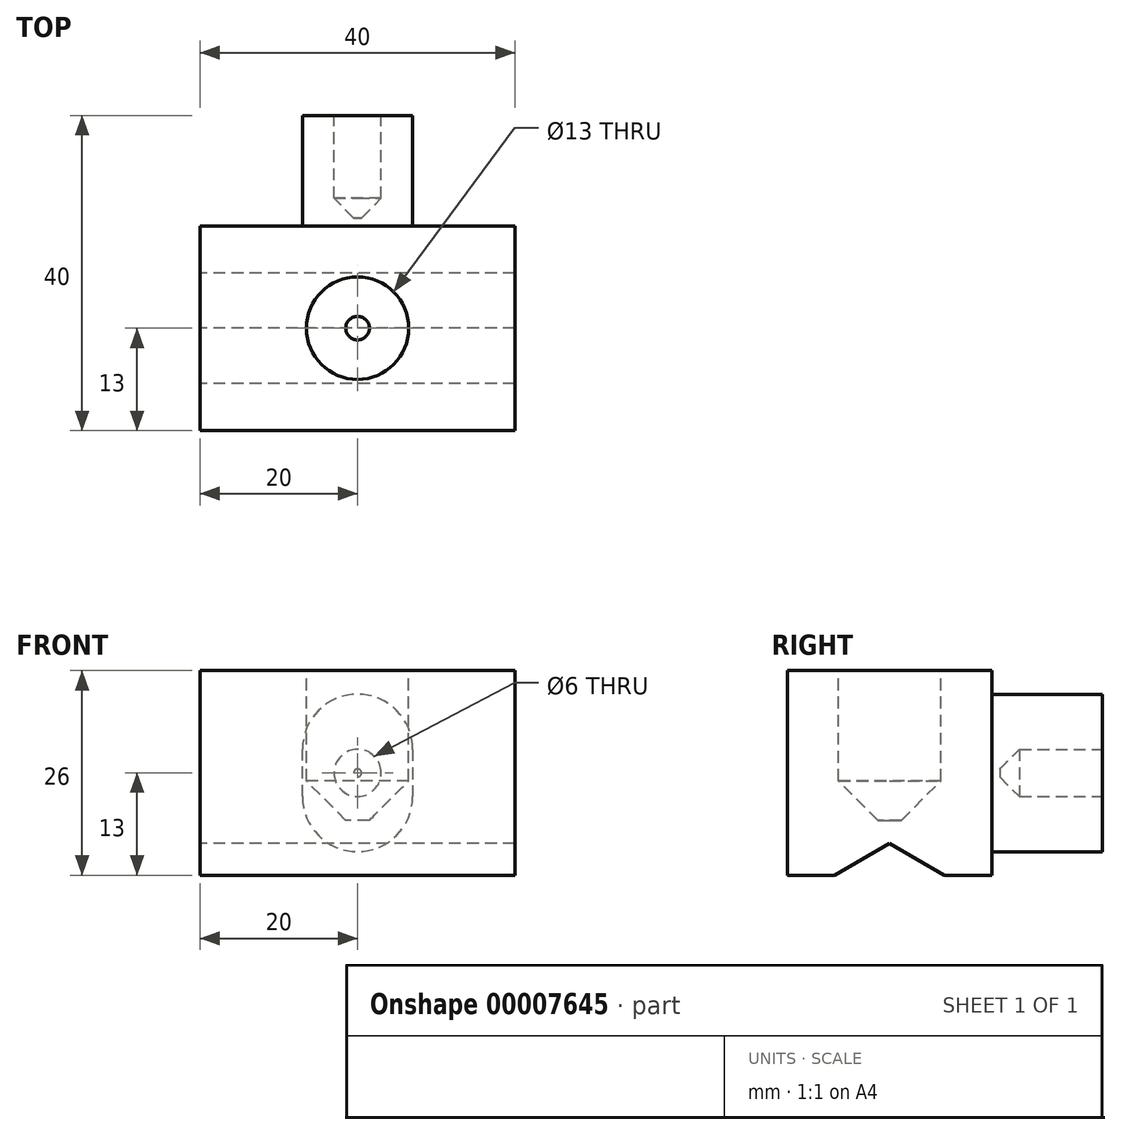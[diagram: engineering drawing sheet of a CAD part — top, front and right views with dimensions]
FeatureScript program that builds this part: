
annotation { "Feature Type Name" : "Feature", "Feature Type Description" : "" }
export const myFeature = defineFeature(function(context is Context, id is Id, definition is map)
    precondition{}
    {
        {
            var Q0;
            Q0=qCreatedBy(makeId("Right.planeOp"),FACE);
            var sketch = newSketch(context, id + "F0", { "sketchPlane" : qUnion([Q0])});
            skLineSegment(sketch, "E0.rect.bottom", {"start": v(-13, -13) * mm, "end": v(-7, -13) * mm});
            skLineSegment(sketch, "E0.rect.top", {"start": v(-13, 13) * mm, "end": v(13, 13) * mm});
            skLineSegment(sketch, "E0.rect.left", {"start": v(-13, -13) * mm, "end": v(-13, 13) * mm});
            skLineSegment(sketch, "E0.rect.right", {"start": v(13, -13) * mm, "end": v(13, 13) * mm});
            skPoint(sketch, "E0.rect.middle", {"position": v(0, 0) * mm});
            skLineSegment(sketch, "E1", {"start": v(0, -8.96) * mm, "end": v(-7, -13) * mm});
            skLineSegment(sketch, "E2", {"start": v(7, -13) * mm, "end": v(0, -8.96) * mm});
            skLineSegment(sketch, "E3.trimOffspring", {"start": v(7, -13) * mm, "end": v(13, -13) * mm});
            skSolve(sketch);
        }
        {
            var Q0;
            Q0 = qSketchRegion(id + "F0", true);
            extrude(context, id + "F1", {"entities" : qUnion([Q0]), "depth" : 40 * mm, "symmetric" : true});
        }
        {
            var Q0;
            Q0=makeQuery(id+"F1.opExtrude","SWEPT_FACE",FACE,{"disambiguationData":[OSD([sQuery(id+"F0.wireOp",EDGE,"E0.rect.top")])]});
            var sketch = newSketch(context, id + "F2", { "sketchPlane" : qUnion([Q0])});
            skCircle(sketch, "E4", {"center": v(0, 0) * mm, "radius": 6.5 * mm});
            skSolve(sketch);
        }
        {
            var Q0;
            Q0 = qSketchRegion(id + "F2", true);
            extrude(context, id + "F3", {"entities" : qUnion([Q0]), "operationType" : NewBodyOperationType.REMOVE, "oppositeDirection" : true, "depth" : 19 * mm});
        }
        {
            var Q0;
            Q0=makeQuery(id+"F3.boolean.opBoolean","COPY",EDGE,{"derivedFrom":makeQuery(id+"F3.opExtrude","CAP_EDGE",EDGE,{"disambiguationData":[OSD([sQuery(id+"F2.wireOp",EDGE,"E4")])],"isStart":false})});
            chamfer(context, id + "F4", {"entities" : qUnion([Q0]), "width" : 5 * mm, "tangentPropagation" : true});
        }
        {
            var Q0;
            Q0=makeQuery(id+"F1.opExtrude","SWEPT_FACE",FACE,{"disambiguationData":[OSD([sQuery(id+"F0.wireOp",EDGE,"E0.rect.right")])]});
            var sketch = newSketch(context, id + "F5", { "sketchPlane" : qUnion([Q0])});
            skLineSegment(sketch, "E5", {"start": v(-7, 3) * mm, "end": v(-7, -3) * mm});
            skArc(sketch, "E6", {"start": v(-7, -3) * mm, "mid": v(0, -10) * mm, "end": v(7, -3) * mm});
            skLineSegment(sketch, "E7", {"start": v(7, -3) * mm, "end": v(7, 3) * mm});
            skArc(sketch, "E8", {"start": v(7, 3) * mm, "mid": v(0, 10) * mm, "end": v(-7, 3) * mm});
            skLineSegment(sketch, "E9", {"start": v(0, 3) * mm, "end": v(0, -3) * mm, "construction": true});
            skSolve(sketch);
        }
        {
            var Q0;
            Q0 = qSketchRegion(id + "F5", true);
            extrude(context, id + "F6", {"entities" : qUnion([Q0]), "operationType" : NewBodyOperationType.ADD, "depth" : 14 * mm});
        }
        {
            var Q0;
            Q0=makeQuery(id+"F6.opExtrude","CAP_FACE",FACE,{"disambiguationData":[OSD([sQuery(id+"F5.wireOp",EDGE,"E5"),sQuery(id+"F5.wireOp",EDGE,"E6"),sQuery(id+"F5.wireOp",EDGE,"E7"),sQuery(id+"F5.wireOp",EDGE,"E8")])],"isStart":false});
            var sketch = newSketch(context, id + "F7", { "sketchPlane" : qUnion([Q0])});
            skCircle(sketch, "E10", {"center": v(0, 0) * mm, "radius": 3 * mm});
            skSolve(sketch);
        }
        {
            var Q0;
            Q0 = qSketchRegion(id + "F7", true);
            extrude(context, id + "F8", {"entities" : qUnion([Q0]), "operationType" : NewBodyOperationType.REMOVE, "oppositeDirection" : true, "depth" : 13 * mm});
        }
        {
            var Q0;
            Q0=makeQuery(id+"F8.boolean.opBoolean","COPY",EDGE,{"derivedFrom":makeQuery(id+"F8.opExtrude","CAP_EDGE",EDGE,{"disambiguationData":[OSD([sQuery(id+"F7.wireOp",EDGE,"E10")])],"isStart":false})});
            chamfer(context, id + "F9", {"entities" : qUnion([Q0]), "width" : 2.5 * mm, "tangentPropagation" : true});
        }
    });
